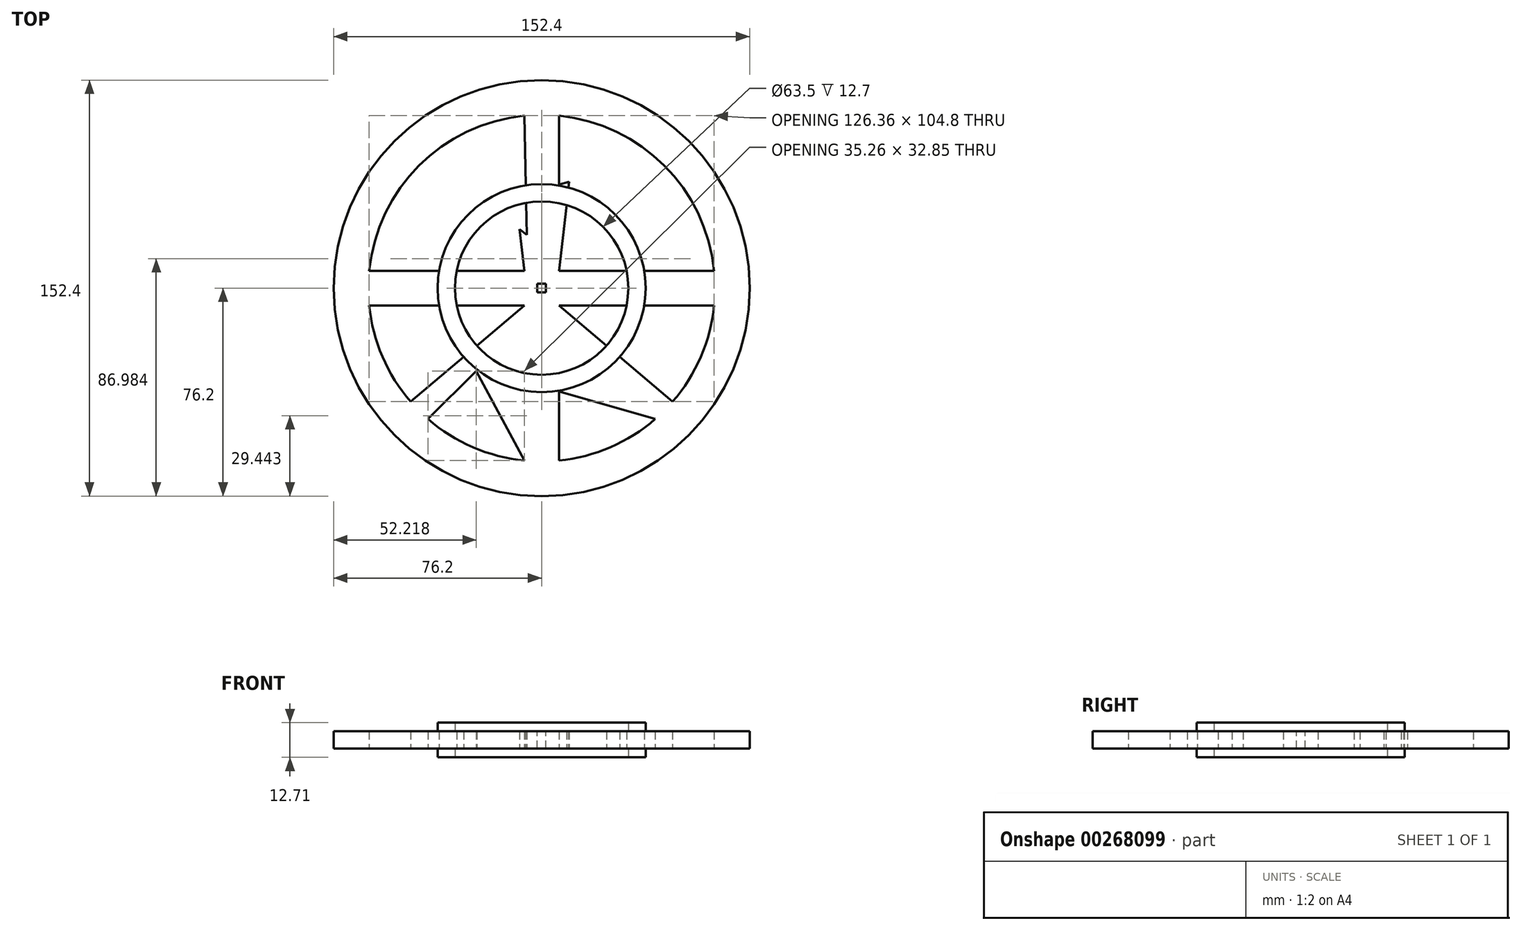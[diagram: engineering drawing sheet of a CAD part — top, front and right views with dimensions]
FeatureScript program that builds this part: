
annotation { "Feature Type Name" : "Feature", "Feature Type Description" : "" }
export const myFeature = defineFeature(function(context is Context, id is Id, definition is map)
    precondition{}
    {
        {
            var Q0;
            Q0=qCreatedBy(makeId("Top.planeOp"),FACE);
            var sketch = newSketch(context, id + "F0", { "sketchPlane" : qUnion([Q0])});
            skCircle(sketch, "E0", {"center": v(0, 0) * mm, "radius": 76.2 * mm});
            skArc(sketch, "E1", {"start": v(-63.18, -6.35) * mm, "mid": v(-58.3, -25.16) * mm, "end": v(-47.96, -41.61) * mm});
            skLineSegment(sketch, "E2.MirrorCS", {"start": v(-63.18, -6.35) * mm, "end": v(-6.35, -6.35) * mm});
            skLineSegment(sketch, "E3", {"start": v(-5.5, 19.55) * mm, "end": v(-6.35, 63.18) * mm});
            skLineSegment(sketch, "E4.MirrorCS", {"start": v(-23.98, -30.33) * mm, "end": v(-6.35, -63.18) * mm});
            skLineSegment(sketch, "E5.MirrorCS", {"start": v(6.35, -37.94) * mm, "end": v(6.35, -63.18) * mm});
            skLineSegment(sketch, "E6", {"start": v(-6.35, 6.35) * mm, "end": v(-12.8, 62.2) * mm});
            skLineSegment(sketch, "E7", {"start": v(-5.5, 19.55) * mm, "end": v(-41.61, 47.96) * mm});
            skLineSegment(sketch, "E8", {"start": v(6.35, 37.94) * mm, "end": v(41.61, 47.96) * mm});
            skLineSegment(sketch, "E9", {"start": v(6.35, 6.35) * mm, "end": v(12.8, 62.2) * mm});
            skLineSegment(sketch, "E10", {"start": v(6.35, -37.94) * mm, "end": v(41.61, -47.96) * mm});
            skLineSegment(sketch, "E11", {"start": v(6.35, -6.35) * mm, "end": v(47.96, -41.61) * mm});
            skLineSegment(sketch, "E12", {"start": v(-6.35, -6.35) * mm, "end": v(-47.96, -41.61) * mm});
            skLineSegment(sketch, "E13", {"start": v(-23.98, -30.33) * mm, "end": v(-41.61, -47.96) * mm});
            skLineSegment(sketch, "E14.trimOffspring", {"start": v(-63.18, 6.35) * mm, "end": v(-6.35, 6.35) * mm});
            skPoint(sketch, "E15.start.orphan", {"position": v(-52, 3.18) * mm});
            skPoint(sketch, "E16.orphan", {"position": v(-52, -6.35) * mm});
            skPoint(sketch, "E17.orphan", {"position": v(-24.14, -30.04) * mm});
            skLineSegment(sketch, "E18.trimOffspring", {"start": v(6.35, -6.35) * mm, "end": v(63.18, -6.35) * mm});
            skLineSegment(sketch, "E19.trimOffspring", {"start": v(6.35, 6.35) * mm, "end": v(63.18, 6.35) * mm});
            skPoint(sketch, "E20.orphan", {"position": v(-5.02, -5.22) * mm});
            skLineSegment(sketch, "E21.trimOffspring", {"start": v(6.35, 37.94) * mm, "end": v(6.35, 63.18) * mm});
            skPoint(sketch, "E22.orphan", {"position": v(6.35, -31.6) * mm});
            skPoint(sketch, "E23.orphan", {"position": v(5.02, -5.22) * mm});
            skPoint(sketch, "E24.start.orphan", {"position": v(0, 44.76) * mm});
            skPoint(sketch, "E25.start.orphan", {"position": v(-52, 0) * mm});
            skPoint(sketch, "E26.orphan", {"position": v(48.28, 6.35) * mm});
            skPoint(sketch, "E27.orphan", {"position": v(48.28, -6.35) * mm});
            skArc(sketch, "E28.trimOffspring", {"start": v(-41.61, -47.96) * mm, "mid": v(-25.16, -58.3) * mm, "end": v(-6.35, -63.18) * mm});
            skArc(sketch, "E29.trimOffspring", {"start": v(6.35, -63.18) * mm, "mid": v(25.16, -58.3) * mm, "end": v(41.61, -47.96) * mm});
            skArc(sketch, "E30.trimOffspring", {"start": v(47.96, -41.61) * mm, "mid": v(58.3, -25.16) * mm, "end": v(63.18, -6.35) * mm});
            skArc(sketch, "E31.trimOffspring", {"start": v(63.18, 6.35) * mm, "mid": v(47.15, 42.54) * mm, "end": v(12.8, 62.2) * mm});
            skArc(sketch, "E32.trimOffspring", {"start": v(-12.8, 62.2) * mm, "mid": v(-47.15, 42.54) * mm, "end": v(-63.18, 6.35) * mm});
            skArc(sketch, "E33.trimOffspring", {"start": v(-6.35, 63.18) * mm, "mid": v(-25.16, 58.3) * mm, "end": v(-41.61, 47.96) * mm});
            skArc(sketch, "E34.trimOffspring", {"start": v(41.61, 47.96) * mm, "mid": v(25.16, 58.3) * mm, "end": v(6.35, 63.18) * mm});
            skSolve(sketch);
        }
        {
            var Q0;
            Q0=makeQuery(id+"F0.imprint","IMPRINT",FACE,{"disambiguationData":[TD([[makeQuery(id+"F0.imprint","IMPRINT",EDGE,{"derivedFrom":sQuery(id+"F0.wireOp",EDGE,"E0")}),1.0]])]});
            extrude(context, id + "F1", {"entities" : qUnion([Q0]), "depth" : 6.35 * mm});
        }
        {
            var Q0;
            Q0=qCreatedBy(makeId("Top.planeOp"),FACE);
            cPlane(context, id + "F2", {"entities" : qUnion([Q0]), "cplaneType" : CPlaneType.OFFSET, "offset" : 3.17 * mm, "width" : 152.4 * mm, "height" : 152.4 * mm});
        }
        {
            var Q0;
            Q0=qCreatedBy(id+"F2.planeOp",FACE);
            var sketch = newSketch(context, id + "F3", { "sketchPlane" : qUnion([Q0])});
            skCircle(sketch, "E35", {"center": v(0, 0) * mm, "radius": 38.1 * mm});
            skCircle(sketch, "E36", {"center": v(0, 0) * mm, "radius": 31.75 * mm});
            skSolve(sketch);
        }
        {
            var Q0;
            Q0=qSketchRegion(id+"F3",true);
            extrude(context, id + "F4", {"entities" : qUnion([Q0]), "operationType" : NewBodyOperationType.ADD, "depth" : 6.35 * mm, "hasSecondDirection" : true, "secondDirectionOppositeDirection" : true, "secondDirectionDepth" : 6.35 * mm});
        }
        {
            var Q0;
            Q0=qCreatedBy(makeId("Top.planeOp"),FACE);
            var sketch = newSketch(context, id + "F5", { "sketchPlane" : qUnion([Q0])});
            skLineSegment(sketch, "E37.bottom", {"start": v(1.59, 1.59) * mm, "end": v(-1.59, 1.59) * mm});
            skLineSegment(sketch, "E37.top", {"start": v(1.59, -1.59) * mm, "end": v(-1.59, -1.59) * mm});
            skLineSegment(sketch, "E37.left", {"start": v(1.59, 1.59) * mm, "end": v(1.59, -1.59) * mm});
            skLineSegment(sketch, "E37.right", {"start": v(-1.59, 1.59) * mm, "end": v(-1.59, -1.59) * mm});
            skPoint(sketch, "E37.middle", {"position": v(0, 0) * mm});
            skSolve(sketch);
        }
        {
            var Q0;
            Q0=qSketchRegion(id+"F5",true);
            extrude(context, id + "F6", {"entities" : qUnion([Q0]), "operationType" : NewBodyOperationType.REMOVE, "endBound" : BoundingType.SYMMETRIC, "oppositeDirection" : true, "depth" : 25.4 * mm});
        }
    });
